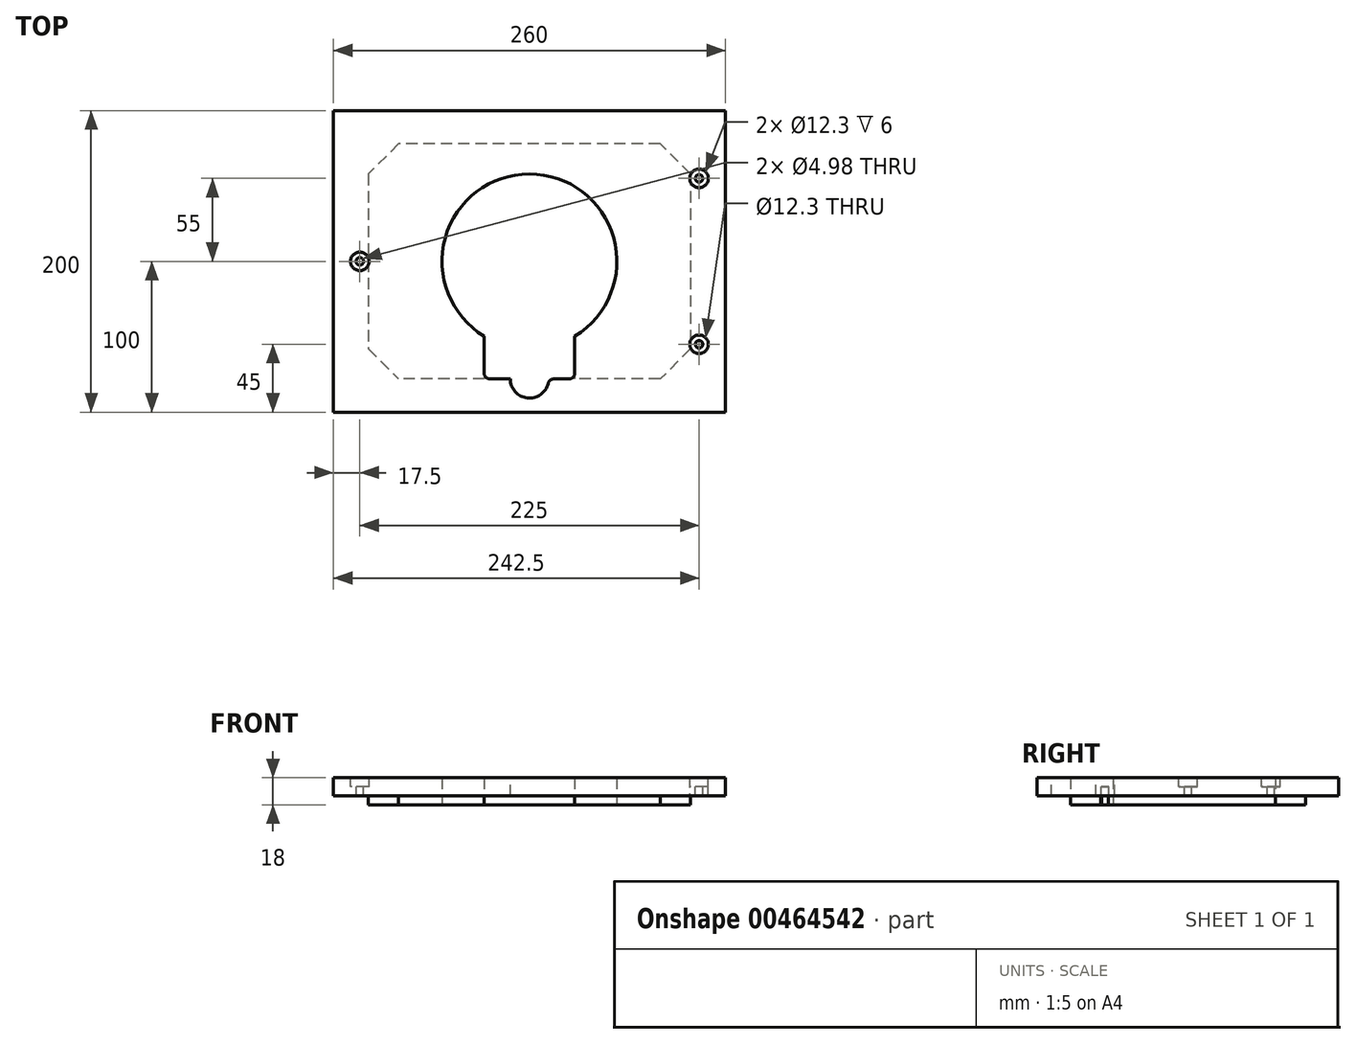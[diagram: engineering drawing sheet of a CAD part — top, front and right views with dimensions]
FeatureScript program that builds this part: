
annotation { "Feature Type Name" : "Feature", "Feature Type Description" : "" }
export const myFeature = defineFeature(function(context is Context, id is Id, definition is map)
    precondition{}
    {
        {
            var Q0;
            Q0=qCreatedBy(makeId("Top.planeOp"),FACE);
            var sketch = newSketch(context, id + "F0", { "sketchPlane" : qUnion([Q0])});
            skLineSegment(sketch, "E0.bottom", {"start": v(86.75, 78) * mm, "end": v(-86.75, 78) * mm});
            skLineSegment(sketch, "E0.top", {"start": v(86.75, -78) * mm, "end": v(30, -78) * mm});
            skLineSegment(sketch, "E0.left", {"start": v(106.75, 58) * mm, "end": v(106.75, -58) * mm});
            skLineSegment(sketch, "E0.right", {"start": v(-106.75, 58) * mm, "end": v(-106.75, -58) * mm});
            skPoint(sketch, "E0.middle", {"position": v(0, 0) * mm});
            skArc(sketch, "E1", {"start": v(30, -49.64) * mm, "mid": v(0, 58) * mm, "end": v(-30, -49.64) * mm});
            skLineSegment(sketch, "E2", {"start": v(-86.75, 78) * mm, "end": v(-106.75, 58) * mm});
            skLineSegment(sketch, "E3", {"start": v(-106.75, -58) * mm, "end": v(-86.75, -78) * mm});
            skLineSegment(sketch, "E4", {"start": v(106.75, -58) * mm, "end": v(86.75, -78) * mm});
            skLineSegment(sketch, "E5", {"start": v(106.75, 58) * mm, "end": v(86.75, 78) * mm});
            skPoint(sketch, "E6.orphan", {"position": v(-106.75, 78) * mm});
            skPoint(sketch, "E7.orphan", {"position": v(-106.75, -78) * mm});
            skPoint(sketch, "E8.orphan", {"position": v(106.75, -78) * mm});
            skPoint(sketch, "E9.orphan", {"position": v(106.75, 78) * mm});
            skPoint(sketch, "E10", {"position": v(-106.75, 0) * mm});
            skPoint(sketch, "E11", {"position": v(0, 78) * mm});
            skPoint(sketch, "E12", {"position": v(106.75, 0) * mm});
            skPoint(sketch, "E13", {"position": v(0, -78) * mm});
            skLineSegment(sketch, "E14", {"start": v(-30, -49.64) * mm, "end": v(-30, -78) * mm});
            skLineSegment(sketch, "E15", {"start": v(30, -49.64) * mm, "end": v(30, -78) * mm});
            skLineSegment(sketch, "E16.trimOffspring", {"start": v(-30, -78) * mm, "end": v(-86.75, -78) * mm});
            skLineSegment(sketch, "E17", {"start": v(-30, -78) * mm, "end": v(30, -78) * mm});
            skLineSegment(sketch, "E18.bottom", {"start": v(130, 100) * mm, "end": v(-130, 100) * mm});
            skLineSegment(sketch, "E18.top", {"start": v(130, -100) * mm, "end": v(-130, -100) * mm});
            skLineSegment(sketch, "E18.left", {"start": v(130, 100) * mm, "end": v(130, -100) * mm});
            skLineSegment(sketch, "E18.right", {"start": v(-130, 100) * mm, "end": v(-130, -100) * mm});
            skSolve(sketch);
        }
        {
            var Q0;
            Q0=makeQuery(id+"F0.imprint","IMPRINT",FACE,{"disambiguationData":[TD([[makeQuery(id+"F0.imprint","IMPRINT",EDGE,{"derivedFrom":sQuery(id+"F0.wireOp",EDGE,"E0.bottom")}),-1.0]])]});
            var Q1;
            Q1=makeQuery(id+"F0.imprint","IMPRINT",FACE,{"disambiguationData":[TD([[makeQuery(id+"F0.imprint","IMPRINT",EDGE,{"derivedFrom":sQuery(id+"F0.wireOp",EDGE,"E0.bottom")}),1.0]])]});
            extrude(context, id + "F1", {"entities" : qUnion([Q0, Q1]), "depth" : 12 * mm});
        }
        {
            var Q0;
            Q0=makeQuery(id+"F0.imprint","IMPRINT",FACE,{"disambiguationData":[TD([[makeQuery(id+"F0.imprint","IMPRINT",EDGE,{"derivedFrom":sQuery(id+"F0.wireOp",EDGE,"E0.bottom")}),1.0]])]});
            extrude(context, id + "F2", {"entities" : qUnion([Q0]), "operationType" : NewBodyOperationType.ADD, "oppositeDirection" : true, "depth" : 6 * mm});
        }
        {
            var Q0;
            Q0=makeQuery(id+"FS88Q7TQ9tGs2v9_1.boolean.opBoolean","MERGE",FACE,{"derivedFrom":[makeQuery(id+"F1.opExtrude","CAP_FACE",FACE,{"disambiguationData":[OSD([sQuery(id+"F0.wireOp",EDGE,"E1"),sQuery(id+"F0.wireOp",EDGE,"E14"),sQuery(id+"F0.wireOp",EDGE,"E15"),sQuery(id+"F0.wireOp",EDGE,"E17"),sQuery(id+"F0.wireOp",EDGE,"E18.bottom"),sQuery(id+"F0.wireOp",EDGE,"E18.top"),sQuery(id+"F0.wireOp",EDGE,"E18.left"),sQuery(id+"F0.wireOp",EDGE,"E18.right")])],"isStart":false}),makeQuery(id+"FS88Q7TQ9tGs2v9_1.opExtrude","CAP_FACE",FACE,{"disambiguationData":[OSD([sQuery(id+"FhswOumCTZEHzoO_1.wireOp",EDGE,"1gW7bGTh-ibTu-7cgR-WawX-hzxgKY7Y0K92.bottom"),sQuery(id+"FhswOumCTZEHzoO_1.wireOp",EDGE,"1gW7bGTh-ibTu-7cgR-WawX-hzxgKY7Y0K92.top"),sQuery(id+"FhswOumCTZEHzoO_1.wireOp",EDGE,"1gW7bGTh-ibTu-7cgR-WawX-hzxgKY7Y0K92.left"),sQuery(id+"FhswOumCTZEHzoO_1.wireOp",EDGE,"1gW7bGTh-ibTu-7cgR-WawX-hzxgKY7Y0K92.right")])],"isStart":true}),makeQuery(id+"FS88Q7TQ9tGs2v9_1.opExtrude","CAP_FACE",FACE,{"disambiguationData":[OSD([sQuery(id+"FhswOumCTZEHzoO_1.wireOp",EDGE,"c69cb45d-b5a4-42ce-9403-945d015bb3670.MirrorCS"),sQuery(id+"FhswOumCTZEHzoO_1.wireOp",EDGE,"81179e80-bb25-45b9-9198-cd79faf67afb0.MirrorCS"),sQuery(id+"FhswOumCTZEHzoO_1.wireOp",EDGE,"c3826fdf-1016-40c0-b954-117f715beb060.MirrorCS"),sQuery(id+"FhswOumCTZEHzoO_1.wireOp",EDGE,"9a182bd8-b6ac-42fd-b3cb-8e6d26f5985d0.MirrorCS")])],"isStart":true})]});
            var sketch = newSketch(context, id + "F3", { "sketchPlane" : qUnion([Q0])});
            skLineSegment(sketch, "E19", {"start": v(0, 100) * mm, "end": v(0, -100) * mm, "construction": true});
            skLineSegment(sketch, "E20", {"start": v(130, 0) * mm, "end": v(-130, 0) * mm, "construction": true});
            skCircle(sketch, "E21", {"center": v(-112.5, 0) * mm, "radius": 2.49 * mm});
            skCircle(sketch, "E22", {"center": v(112.5, 55) * mm, "radius": 2.49 * mm});
            skLineSegment(sketch, "E23", {"start": v(112.5, 100) * mm, "end": v(112.5, -100) * mm, "construction": true});
            skCircle(sketch, "E24.MirrorC", {"center": v(112.5, -55) * mm, "radius": 2.49 * mm});
            skCircle(sketch, "E25", {"center": v(-112.5, 0) * mm, "radius": 6.15 * mm});
            skCircle(sketch, "E26", {"center": v(112.5, 55) * mm, "radius": 6.15 * mm});
            skCircle(sketch, "E27.MirrorC", {"center": v(112.5, -55) * mm, "radius": 6.15 * mm});
            skSolve(sketch);
        }
        {
            var Q0;
            Q0=makeQuery(id+"F3.imprint","IMPRINT",FACE,{"disambiguationData":[TD([[makeQuery(id+"F3.imprint","IMPRINT",EDGE,{"derivedFrom":sQuery(id+"F3.wireOp",EDGE,"E21")}),-1.0]])]});
            var Q1;
            Q1=makeQuery(id+"F3.imprint","IMPRINT",FACE,{"disambiguationData":[TD([[makeQuery(id+"F3.imprint","IMPRINT",EDGE,{"derivedFrom":sQuery(id+"F3.wireOp",EDGE,"E21")}),1.0]])]});
            var Q2;
            Q2=makeQuery(id+"F3.imprint","IMPRINT",FACE,{"disambiguationData":[TD([[makeQuery(id+"F3.imprint","IMPRINT",EDGE,{"derivedFrom":sQuery(id+"F3.wireOp",EDGE,"E22")}),-1.0]])]});
            var Q3;
            Q3=makeQuery(id+"F3.imprint","IMPRINT",FACE,{"disambiguationData":[TD([[makeQuery(id+"F3.imprint","IMPRINT",EDGE,{"derivedFrom":sQuery(id+"F3.wireOp",EDGE,"E22")}),1.0]])]});
            var Q4;
            Q4=makeQuery(id+"F3.imprint","IMPRINT",FACE,{"disambiguationData":[TD([[makeQuery(id+"F3.imprint","IMPRINT",EDGE,{"derivedFrom":sQuery(id+"F3.wireOp",EDGE,"E24.MirrorC")}),-1.0]])]});
            var Q5;
            Q5=makeQuery(id+"F3.imprint","IMPRINT",FACE,{"disambiguationData":[TD([[makeQuery(id+"F3.imprint","IMPRINT",EDGE,{"derivedFrom":sQuery(id+"F3.wireOp",EDGE,"E24.MirrorC")}),1.0]])]});
            extrude(context, id + "F4", {"entities" : qUnion([Q0, Q1, Q2, Q3, Q4, Q5]), "operationType" : NewBodyOperationType.REMOVE, "oppositeDirection" : true, "depth" : 6 * mm});
        }
        {
            var Q0;
            Q0=makeQuery(id+"F3.imprint","IMPRINT",FACE,{"disambiguationData":[TD([[makeQuery(id+"F3.imprint","IMPRINT",EDGE,{"derivedFrom":sQuery(id+"F3.wireOp",EDGE,"E21")}),1.0]])]});
            var Q1;
            Q1=makeQuery(id+"F3.imprint","IMPRINT",FACE,{"disambiguationData":[TD([[makeQuery(id+"F3.imprint","IMPRINT",EDGE,{"derivedFrom":sQuery(id+"F3.wireOp",EDGE,"E22")}),1.0]])]});
            var Q2;
            Q2=makeQuery(id+"F3.imprint","IMPRINT",FACE,{"disambiguationData":[TD([[makeQuery(id+"F3.imprint","IMPRINT",EDGE,{"derivedFrom":sQuery(id+"F3.wireOp",EDGE,"E24.MirrorC")}),-1.0]])]});
            extrude(context, id + "F5", {"entities" : qUnion([Q0, Q1, Q2]), "operationType" : NewBodyOperationType.REMOVE, "endBound" : BoundingType.THROUGH_ALL, "oppositeDirection" : true, "depth" : 25 * mm});
        }
        {
            var Q0;
            Q0=makeQuery(id+"F1.opExtrude","SWEPT_EDGE",EDGE,{"disambiguationData":[OSD([sQuery(id+"F0.wireOp",EDGE,"E14"),sQuery(id+"F0.wireOp",EDGE,"E16.trimOffspring"),sQuery(id+"F0.wireOp",EDGE,"E17")])]});
            var Q1;
            Q1=makeQuery(id+"F1.opExtrude","SWEPT_EDGE",EDGE,{"disambiguationData":[OSD([sQuery(id+"F0.wireOp",EDGE,"E0.top"),sQuery(id+"F0.wireOp",EDGE,"E15"),sQuery(id+"F0.wireOp",EDGE,"E17")])]});
            fillet(context, id + "F6", {"entities" : qUnion([Q0, Q1]), "radius" : 3.8 * mm, "tangentPropagation" : true, "allowEdgeOverflow" : false});
        }
        {
            var Q0;
            Q0=makeQuery(id+"F1.opExtrude","CAP_FACE",FACE,{"disambiguationData":[OSD([sQuery(id+"F0.wireOp",EDGE,"E1"),sQuery(id+"F0.wireOp",EDGE,"E14"),sQuery(id+"F0.wireOp",EDGE,"E15"),sQuery(id+"F0.wireOp",EDGE,"E17"),sQuery(id+"F0.wireOp",EDGE,"E18.bottom"),sQuery(id+"F0.wireOp",EDGE,"E18.top"),sQuery(id+"F0.wireOp",EDGE,"E18.left"),sQuery(id+"F0.wireOp",EDGE,"E18.right")])],"isStart":false});
            var sketch = newSketch(context, id + "F7", { "sketchPlane" : qUnion([Q0])});
            skArc(sketch, "E28", {"start": v(-12.7, -78) * mm, "mid": v(0, -90.7) * mm, "end": v(12.7, -78) * mm});
            skLineSegment(sketch, "E29", {"start": v(-12.7, -78) * mm, "end": v(12.7, -78) * mm});
            skSolve(sketch);
        }
        {
            var Q0;
            Q0 = qSketchRegion(id + "F7", true);
            extrude(context, id + "F8", {"entities" : qUnion([Q0]), "operationType" : NewBodyOperationType.REMOVE, "endBound" : BoundingType.THROUGH_ALL, "oppositeDirection" : true, "depth" : 25.4 * mm, "offsetDistance" : 25.4 * mm});
        }
        {
            var Q0;
            {var subQ0=sQuery(id+"F7.wireOp",EDGE,"E29");var subQ1=sQuery(id+"F7.wireOp",EDGE,"E28");var subQ2=sQuery(id+"F0.wireOp",EDGE,"E17");Q0=makeQuery(id+"F8.boolean.opBoolean","COPY",EDGE,{"derivedFrom":makeQuery(id+"F8.opExtrude","SWEPT_EDGE",EDGE,{"disambiguationData":[OSD([subQ2,subQ1,subQ0]),TDD([makeQuery(id+"F7.imprint","INTERSECT",VERTEX,{"disambiguationData":[OD(0.0)],"derivedFrom":[makeQuery(id+"F1.opExtrude","CAP_EDGE",EDGE,{"disambiguationData":[OSD([subQ2])],"isStart":false}),subQ1,subQ0]})])]})});}
            var Q1;
            {var subQ0=sQuery(id+"F7.wireOp",EDGE,"E29");var subQ1=sQuery(id+"F7.wireOp",EDGE,"E28");var subQ2=sQuery(id+"F0.wireOp",EDGE,"E17");Q1=makeQuery(id+"F8.boolean.opBoolean","COPY",EDGE,{"derivedFrom":makeQuery(id+"F8.opExtrude","SWEPT_EDGE",EDGE,{"disambiguationData":[OSD([subQ2,subQ1,subQ0]),TDD([makeQuery(id+"F7.imprint","INTERSECT",VERTEX,{"disambiguationData":[OD(1.0)],"derivedFrom":[makeQuery(id+"F1.opExtrude","CAP_EDGE",EDGE,{"disambiguationData":[OSD([subQ2])],"isStart":false}),subQ1,subQ0]})])]})});}
            fillet(context, id + "F9", {"entities" : qUnion([Q0, Q1]), "radius" : 3.8 * mm, "tangentPropagation" : true, "allowEdgeOverflow" : false});
        }
    });
